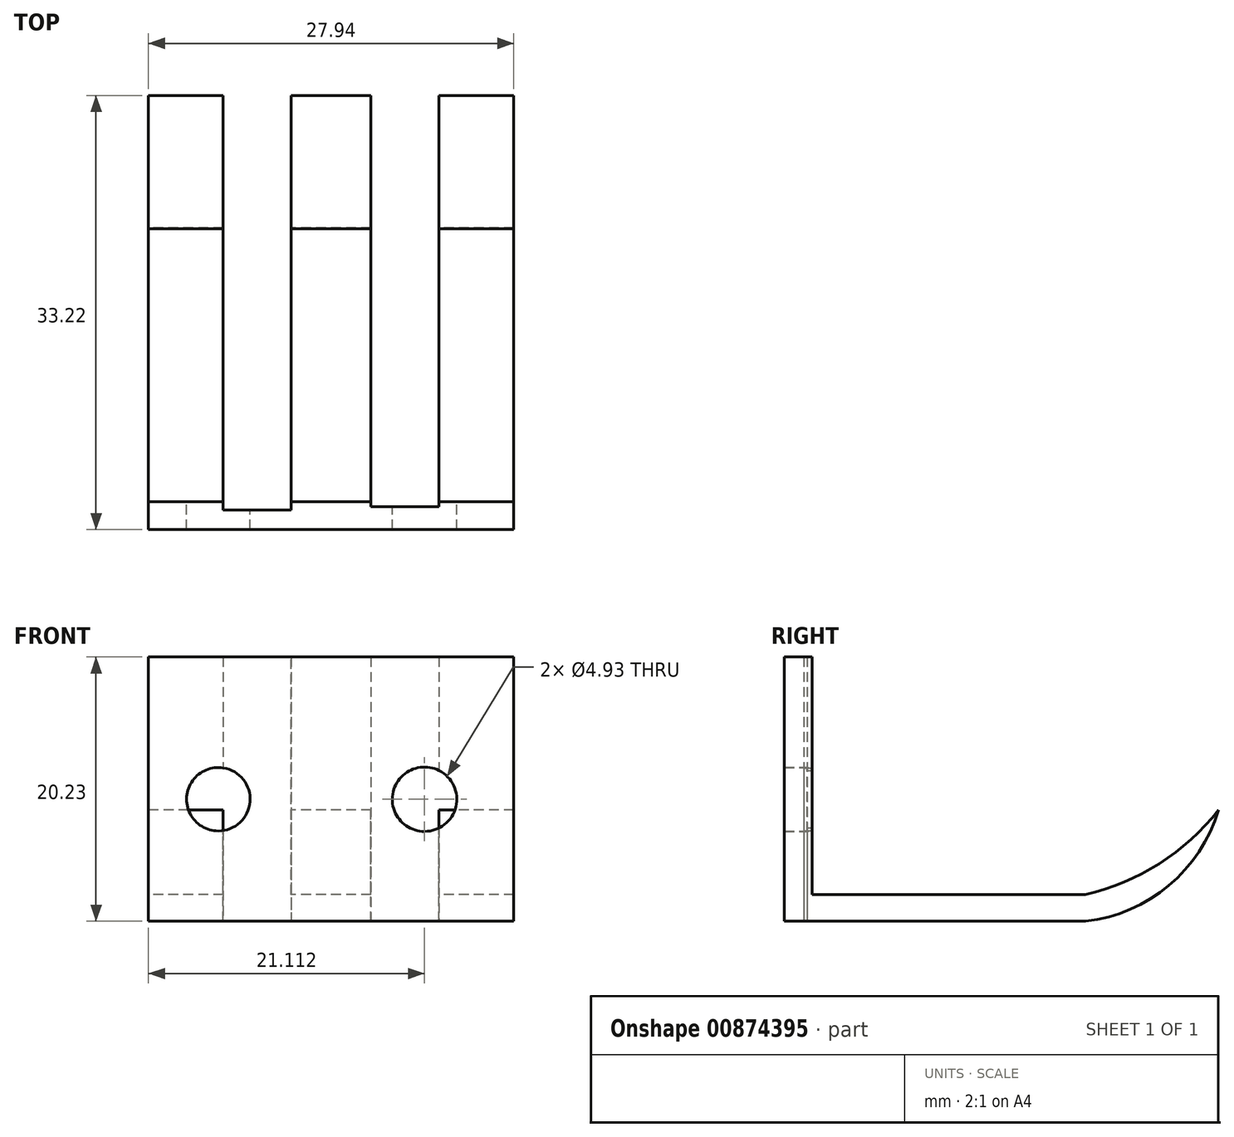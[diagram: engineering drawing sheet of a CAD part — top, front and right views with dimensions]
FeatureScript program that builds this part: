
annotation { "Feature Type Name" : "Feature", "Feature Type Description" : "" }
export const myFeature = defineFeature(function(context is Context, id is Id, definition is map)
    precondition{}
    {
        {
            var Q0;
            Q0=qCreatedBy(makeId("Right.planeOp"),FACE);
            var sketch = newSketch(context, id + "F0", { "sketchPlane" : qUnion([Q0])});
            skArc(sketch, "E0", {"start": v(-10.15, 0) * mm, "mid": v(-3.8, 2.74) * mm, "end": v(0, 8.5) * mm});
            skLineSegment(sketch, "E1", {"start": v(-10.15, 0) * mm, "end": v(-33.22, 0) * mm});
            skLineSegment(sketch, "E2", {"start": v(-33.22, 0) * mm, "end": v(-33.22, 20.23) * mm});
            skLineSegment(sketch, "E3", {"start": v(-33.22, 20.23) * mm, "end": v(-31.08, 20.23) * mm});
            skLineSegment(sketch, "E4", {"start": v(-31.08, 20.23) * mm, "end": v(-31.08, 2.05) * mm});
            skLineSegment(sketch, "E5", {"start": v(-31.08, 2.05) * mm, "end": v(-10.2, 2.05) * mm});
            skArc(sketch, "E6", {"start": v(-10.2, 2.05) * mm, "mid": v(-4.54, 4.4) * mm, "end": v(0, 8.5) * mm});
            skSolve(sketch);
        }
        {
            var Q0;
            Q0 = qSketchRegion(id + "F0", true);
            extrude(context, id + "F1", {"entities" : qUnion([Q0]), "depth" : 27.94 * mm, "offsetDistance" : 25.4 * mm});
        }
        {
            var Q0;
            Q0=makeQuery(id+"F1.opExtrude","SWEPT_FACE",FACE,{"disambiguationData":[OSD([sQuery(id+"F0.wireOp",EDGE,"E4")])]});
            var sketch = newSketch(context, id + "F2", { "sketchPlane" : qUnion([Q0])});
            skCircle(sketch, "E7", {"center": v(-5.34, 9.34) * mm, "radius": 2.43 * mm});
            skCircle(sketch, "E8", {"center": v(-21.11, 9.34) * mm, "radius": 2.46 * mm});
            skSolve(sketch);
        }
        {
            var Q0;
            Q0 = qSketchRegion(id + "F2", true);
            extrude(context, id + "F3", {"entities" : qUnion([Q0]), "operationType" : NewBodyOperationType.REMOVE, "oppositeDirection" : true, "depth" : 5.08 * mm, "offsetDistance" : 25.4 * mm});
        }
        {
            var Q0;
            Q0=qCreatedBy(makeId("Top.planeOp"),FACE);
            var sketch = newSketch(context, id + "F4", { "sketchPlane" : qUnion([Q0])});
            skLineSegment(sketch, "E9", {"start": v(5.72, 0) * mm, "end": v(5.72, -31.7) * mm});
            skLineSegment(sketch, "E10", {"start": v(5.72, -31.7) * mm, "end": v(10.92, -31.7) * mm});
            skLineSegment(sketch, "E11", {"start": v(10.92, -31.7) * mm, "end": v(10.92, 0) * mm});
            skLineSegment(sketch, "E12", {"start": v(10.92, 0) * mm, "end": v(5.72, 0) * mm});
            skLineSegment(sketch, "E13.bottom", {"start": v(17.02, 0) * mm, "end": v(22.23, 0) * mm});
            skLineSegment(sketch, "E13.top", {"start": v(17.02, -31.47) * mm, "end": v(22.23, -31.47) * mm});
            skLineSegment(sketch, "E13.left", {"start": v(17.02, 0) * mm, "end": v(17.02, -31.47) * mm});
            skLineSegment(sketch, "E13.right", {"start": v(22.23, 0) * mm, "end": v(22.23, -31.47) * mm});
            skSolve(sketch);
        }
        {
            var Q0;
            Q0 = qSketchRegion(id + "F4", true);
            extrude(context, id + "F5", {"entities" : qUnion([Q0]), "operationType" : NewBodyOperationType.REMOVE, "depth" : 23.62 * mm, "offsetDistance" : 25.4 * mm});
        }
    });
